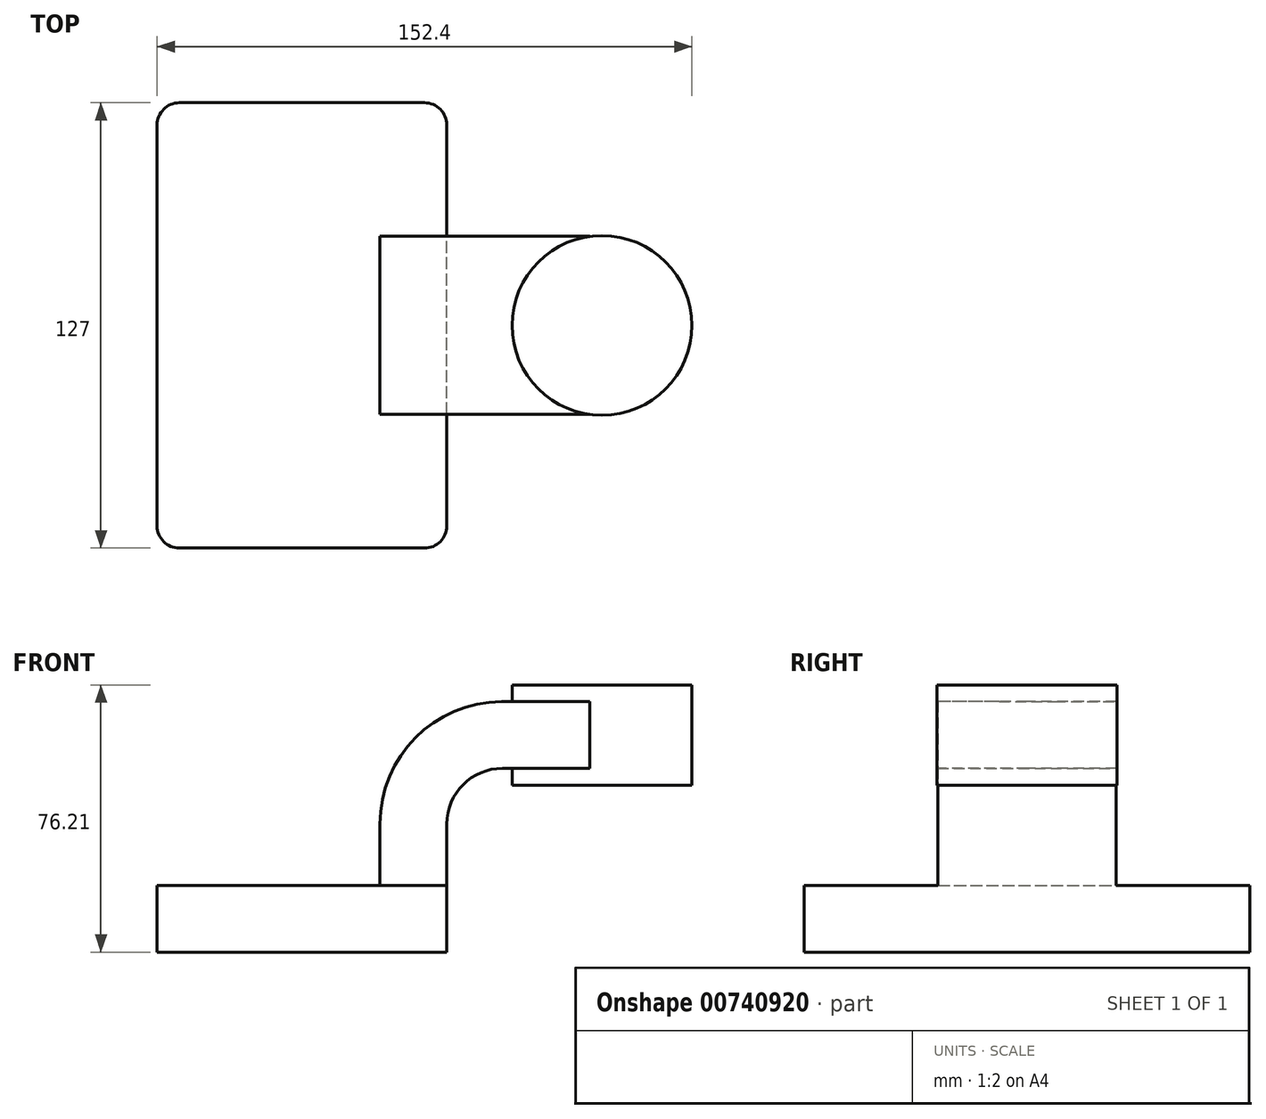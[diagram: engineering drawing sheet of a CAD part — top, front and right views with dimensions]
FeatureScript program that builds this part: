
annotation { "Feature Type Name" : "Feature", "Feature Type Description" : "" }
export const myFeature = defineFeature(function(context is Context, id is Id, definition is map)
    precondition{}
    {
        {
            var Q0;
            Q0=qCreatedBy(makeId("Front.planeOp"),FACE);
            var sketch = newSketch(context, id + "F0", { "sketchPlane" : qUnion([Q0])});
            skLineSegment(sketch, "E0.bottom", {"start": v(-41.28, 9.52) * mm, "end": v(41.27, 9.53) * mm});
            skLineSegment(sketch, "E0.top", {"start": v(-41.28, -9.53) * mm, "end": v(41.28, -9.53) * mm});
            skLineSegment(sketch, "E0.left", {"start": v(-41.28, 9.52) * mm, "end": v(-41.27, -9.53) * mm});
            skLineSegment(sketch, "E0.right", {"start": v(41.28, 9.53) * mm, "end": v(41.28, -9.52) * mm});
            skPoint(sketch, "E0.middle", {"position": v(0, 0) * mm});
            skLineSegment(sketch, "E1.bottom", {"start": v(111.13, 38.1) * mm, "end": v(60.33, 38.1) * mm});
            skLineSegment(sketch, "E1.top", {"start": v(111.13, 66.68) * mm, "end": v(60.33, 66.68) * mm});
            skLineSegment(sketch, "E1.left", {"start": v(111.13, 38.1) * mm, "end": v(111.13, 66.68) * mm});
            skLineSegment(sketch, "E1.right", {"start": v(60.33, 38.1) * mm, "end": v(60.33, 66.68) * mm});
            skPoint(sketch, "E1.middle", {"position": v(85.73, 52.39) * mm});
            skLineSegment(sketch, "E2", {"start": v(41.27, 9.53) * mm, "end": v(41.27, 27) * mm});
            skArc(sketch, "E3", {"start": v(41.27, 27) * mm, "mid": v(45.92, 38.23) * mm, "end": v(57.15, 42.88) * mm});
            skLineSegment(sketch, "E4", {"start": v(57.15, 42.88) * mm, "end": v(85.5, 42.88) * mm});
            skLineSegment(sketch, "E5.0", {"start": v(57.15, 61.93) * mm, "end": v(85.5, 61.93) * mm});
            skArc(sketch, "E5.1", {"start": v(22.22, 27) * mm, "mid": v(32.45, 51.7) * mm, "end": v(57.15, 61.93) * mm});
            skLineSegment(sketch, "E5.2", {"start": v(22.22, 9.53) * mm, "end": v(22.22, 27) * mm});
            skLineSegment(sketch, "E6", {"start": v(85.5, 38.1) * mm, "end": v(85.5, 66.68) * mm});
            skFitSpline(sketch, "E7", {"points": [v(-41.28, 9.52) * mm, v(57.15, 61.93) * mm], "startDerivative": vector(2.06, 93.96) * mm, "endDerivative": vector(171.45, 0.5) * mm});
            skSolve(sketch);
        }
        {
            var Q0;
            Q0=makeQuery(id+"F0.imprint","IMPRINT",FACE,{"disambiguationData":[TD([[makeQuery(id+"F0.imprint","IMPRINT",EDGE,{"derivedFrom":sQuery(id+"F0.wireOp",EDGE,"E0.top")}),1.0]])]});
            extrude(context, id + "F1", {"entities" : qUnion([Q0]), "endBound" : BoundingType.SYMMETRIC, "depth" : 127 * mm, "offsetDistance" : 25.4 * mm});
        }
        {
            var Q0;
            {var subQ5=sQuery(id+"F0.wireOp",EDGE,"E2");Q0=makeQuery(id+"F0.imprint","IMPRINT",FACE,{"disambiguationData":[TD([[makeQuery(id+"F0.imprint","IMPRINT",EDGE,{"derivedFrom":subQ5}),1.0]])]});}
            var Q1;
            {var subQ0=sQuery(id+"F0.wireOp",EDGE,"E4");var subQ1=sQuery(id+"F0.wireOp",EDGE,"E1.right");var subQ2=makeQuery(id+"F0.imprint","INTERSECT",VERTEX,{"derivedFrom":[subQ1,subQ0]});Q1=makeQuery(id+"F0.imprint","IMPRINT",FACE,{"disambiguationData":[TD([[makeQuery(id+"F0.imprint","IMPRINT",EDGE,{"disambiguationData":[TD([[subQ2,-1.0]])],"derivedFrom":subQ1}),-1.0]])]});}
            extrude(context, id + "F2", {"entities" : qUnion([Q0, Q1]), "operationType" : NewBodyOperationType.ADD, "endBound" : BoundingType.SYMMETRIC, "depth" : 50.8 * mm, "offsetDistance" : 25.4 * mm});
        }
        {
            var Q0;
            {var subQ4=sQuery(id+"F0.wireOp",EDGE,"E5.1");Q0=makeQuery(id+"F0.imprint","IMPRINT",FACE,{"disambiguationData":[TD([[makeQuery(id+"F0.imprint","IMPRINT",EDGE,{"derivedFrom":subQ4}),1.0]])]});}
            extrude(context, id + "F3", {"entities" : qUnion([Q0]), "operationType" : NewBodyOperationType.ADD, "endBound" : BoundingType.SYMMETRIC, "depth" : 15.88 * mm, "offsetDistance" : 25.4 * mm});
        }
        {
            var Q0;
            {var subQ4=sQuery(id+"F0.wireOp",EDGE,"E1.left");Q0=makeQuery(id+"F0.imprint","IMPRINT",FACE,{"disambiguationData":[TD([[makeQuery(id+"F0.imprint","IMPRINT",EDGE,{"derivedFrom":subQ4}),1.0]])]});}
            var Q1;
            Q1=sQuery(id+"F0.wireOp",EDGE,"E6");
            revolve(context, id + "F4", {"operationType" : NewBodyOperationType.ADD, "surfaceOperationType" : NewSurfaceOperationType.NEW, "entities" : qUnion([Q0]), "axis" : qUnion([Q1]), "revolveType" : RevolveType.FULL});
        }
        {
            var Q0;
            Q0=makeQuery(id+"F1.opExtrude","CAP_EDGE",EDGE,{"disambiguationData":[OSD([sQuery(id+"F0.wireOp",EDGE,"E0.right")])],"isStart":false});
            var Q1;
            Q1=makeQuery(id+"F1.opExtrude","CAP_EDGE",EDGE,{"disambiguationData":[OSD([sQuery(id+"F0.wireOp",EDGE,"E0.left")])],"isStart":false});
            var Q2;
            Q2=makeQuery(id+"F1.opExtrude","CAP_EDGE",EDGE,{"disambiguationData":[OSD([sQuery(id+"F0.wireOp",EDGE,"E0.right")])],"isStart":true});
            var Q3;
            Q3=makeQuery(id+"F1.opExtrude","CAP_EDGE",EDGE,{"disambiguationData":[OSD([sQuery(id+"F0.wireOp",EDGE,"E0.left")])],"isStart":true});
            fillet(context, id + "F5", {"entities" : qUnion([Q0, Q1, Q2, Q3]), "radius" : 6.35 * mm, "tangentPropagation" : true, "allowEdgeOverflow" : false});
        }
    });
